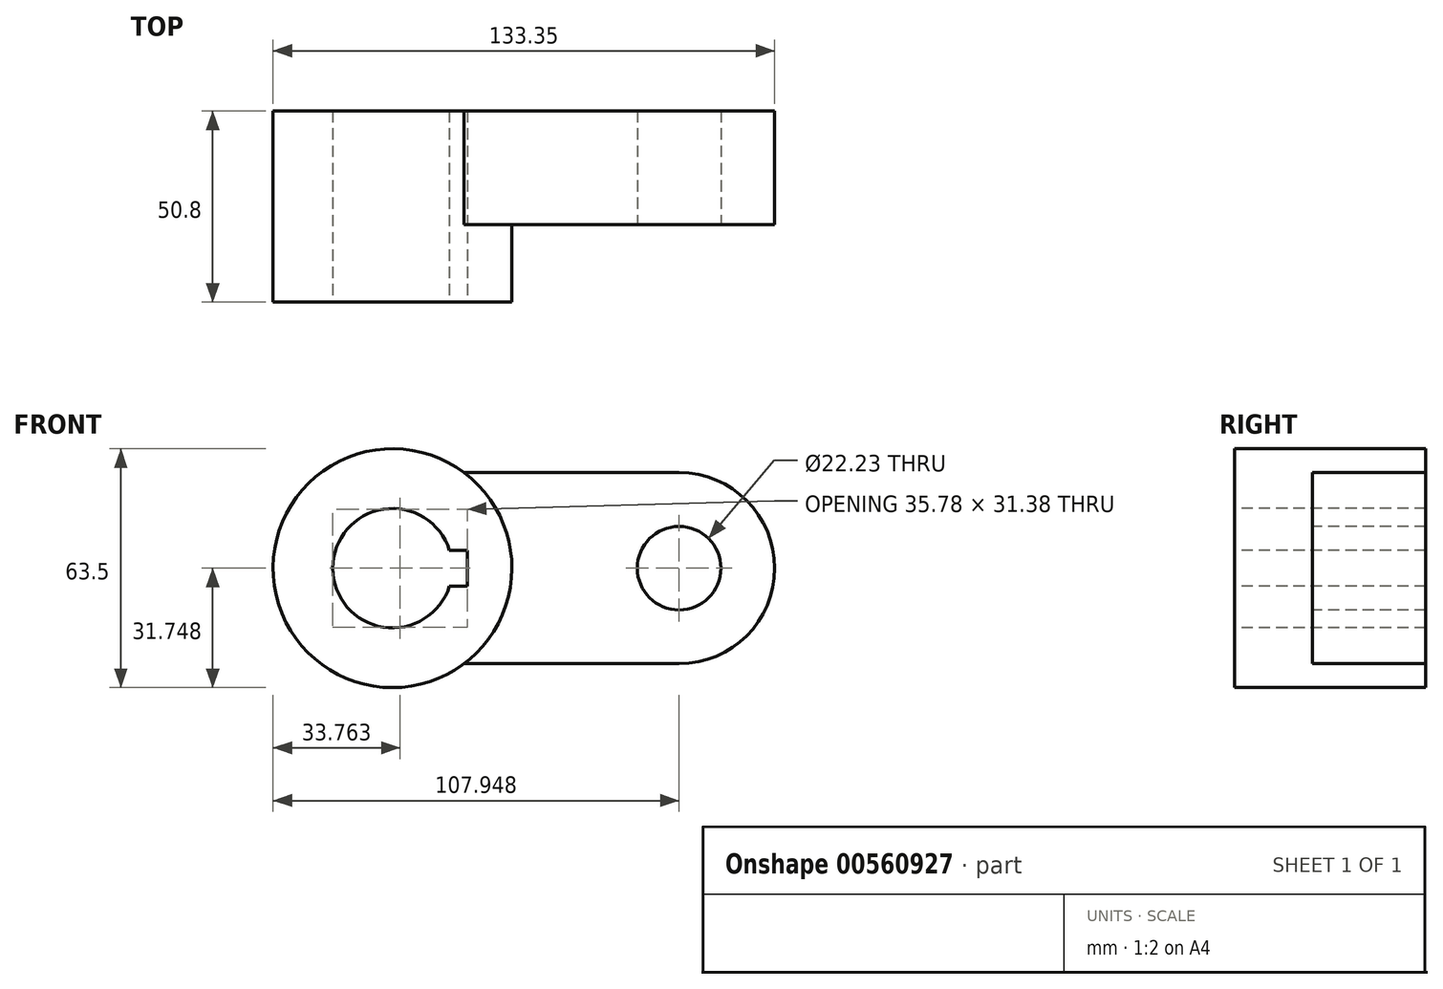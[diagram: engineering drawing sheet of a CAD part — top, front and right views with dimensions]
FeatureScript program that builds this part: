
annotation { "Feature Type Name" : "Feature", "Feature Type Description" : "" }
export const myFeature = defineFeature(function(context is Context, id is Id, definition is map)
    precondition{}
    {
        {
            var Q0;
            Q0=qCreatedBy(makeId("Front.planeOp"),FACE);
            var sketch = newSketch(context, id + "F0", { "sketchPlane" : qUnion([Q0])});
            skLineSegment(sketch, "E0.bottom", {"start": v(-31.26, 34.66) * mm, "end": v(44.94, 34.66) * mm});
            skLineSegment(sketch, "E0.top", {"start": v(-31.26, -16.14) * mm, "end": v(44.94, -16.14) * mm});
            skLineSegment(sketch, "E0.left", {"start": v(-31.26, 34.66) * mm, "end": v(-31.26, -16.14) * mm});
            skLineSegment(sketch, "E0.right", {"start": v(44.94, 34.66) * mm, "end": v(44.94, -16.14) * mm});
            skSolve(sketch);
        }
        {
            var Q0;
            Q0 = qSketchRegion(id + "F0", true);
            extrude(context, id + "F1", {"entities" : qUnion([Q0]), "depth" : 30.16 * mm, "offsetDistance" : 25.4 * mm});
        }
        {
            var Q0;
            Q0=makeQuery(id+"F1.opExtrude","CAP_FACE",FACE,{"disambiguationData":[OSD([sQuery(id+"F0.wireOp",EDGE,"E0.bottom"),sQuery(id+"F0.wireOp",EDGE,"E0.top"),sQuery(id+"F0.wireOp",EDGE,"E0.left"),sQuery(id+"F0.wireOp",EDGE,"E0.right")])],"isStart":true});
            var sketch = newSketch(context, id + "F2", { "sketchPlane" : qUnion([Q0])});
            skArc(sketch, "E1", {"start": v(-44.94, 34.66) * mm, "mid": v(-70.34, 9.26) * mm, "end": v(-44.94, -16.14) * mm});
            skSolve(sketch);
        }
        {
            var Q0;
            Q0=makeQuery(id+"F2.imprint","IMPRINT",FACE,{"disambiguationData":[TD([[makeQuery(id+"F2.imprint","IMPRINT",EDGE,{"derivedFrom":sQuery(id+"F2.wireOp",EDGE,"E1")}),1.0]])]});
            extrude(context, id + "F3", {"entities" : qUnion([Q0]), "operationType" : NewBodyOperationType.ADD, "oppositeDirection" : true, "depth" : 30.16 * mm, "offsetDistance" : 25.4 * mm});
        }
        {
            var Q0;
            {var subQ0=sQuery(id+"F0.wireOp",EDGE,"E0.right");Q0=makeQuery(id+"F3.boolean.opBoolean","MERGE",FACE,{"derivedFrom":[makeQuery(id+"F1.opExtrude","CAP_FACE",FACE,{"disambiguationData":[OSD([sQuery(id+"F0.wireOp",EDGE,"E0.bottom"),sQuery(id+"F0.wireOp",EDGE,"E0.top"),sQuery(id+"F0.wireOp",EDGE,"E0.left"),subQ0])],"isStart":false}),makeQuery(id+"F3.opExtrude","CAP_FACE",FACE,{"disambiguationData":[OSD([subQ0,sQuery(id+"F2.wireOp",EDGE,"E1")])],"isStart":false})]});}
            var sketch = newSketch(context, id + "F4", { "sketchPlane" : qUnion([Q0])});
            skCircle(sketch, "E2", {"center": v(44.94, 9.26) * mm, "radius": 11.11 * mm});
            skSolve(sketch);
        }
        {
            var Q0;
            Q0=makeQuery(id+"F4.imprint","IMPRINT",FACE,{"disambiguationData":[TD([[makeQuery(id+"F4.imprint","IMPRINT",EDGE,{"derivedFrom":sQuery(id+"F4.wireOp",EDGE,"E2")}),1.0]])]});
            extrude(context, id + "F5", {"entities" : qUnion([Q0]), "operationType" : NewBodyOperationType.REMOVE, "oppositeDirection" : true, "depth" : 30.16 * mm, "offsetDistance" : 25.4 * mm});
        }
        {
            var Q0;
            {var subQ0=sQuery(id+"F0.wireOp",EDGE,"E0.right");Q0=makeQuery(id+"F3.boolean.opBoolean","MERGE",FACE,{"derivedFrom":[makeQuery(id+"F1.opExtrude","CAP_FACE",FACE,{"disambiguationData":[OSD([sQuery(id+"F0.wireOp",EDGE,"E0.bottom"),sQuery(id+"F0.wireOp",EDGE,"E0.top"),sQuery(id+"F0.wireOp",EDGE,"E0.left"),subQ0])],"isStart":false}),makeQuery(id+"F3.opExtrude","CAP_FACE",FACE,{"disambiguationData":[OSD([subQ0,sQuery(id+"F2.wireOp",EDGE,"E1")])],"isStart":false})]});}
            var sketch = newSketch(context, id + "F6", { "sketchPlane" : qUnion([Q0])});
            skCircle(sketch, "E3", {"center": v(-31.26, 9.26) * mm, "radius": 31.75 * mm});
            skSolve(sketch);
        }
        {
            var Q0;
            {var subQ5=makeQuery(id+"F1.opExtrude","CAP_EDGE",EDGE,{"disambiguationData":[OSD([sQuery(id+"F0.wireOp",EDGE,"E0.left")])],"isStart":false});Q0=makeQuery(id+"F6.imprint","IMPRINT",FACE,{"disambiguationData":[TD([[makeQuery(id+"F6.imprint","IMPRINT",EDGE,{"derivedFrom":subQ5}),-1.0]])]});}
            var Q1;
            {var subQ5=makeQuery(id+"F1.opExtrude","CAP_EDGE",EDGE,{"disambiguationData":[OSD([sQuery(id+"F0.wireOp",EDGE,"E0.left")])],"isStart":false});Q1=makeQuery(id+"F6.imprint","IMPRINT",FACE,{"disambiguationData":[TD([[makeQuery(id+"F6.imprint","IMPRINT",EDGE,{"derivedFrom":subQ5}),1.0]])]});}
            extrude(context, id + "F7", {"entities" : qUnion([Q0, Q1]), "operationType" : NewBodyOperationType.ADD, "depth" : 20.64 * mm, "offsetDistance" : 25.4 * mm});
        }
        {
            var Q0;
            Q0=makeQuery(id+"F7.opExtrude","CAP_FACE",FACE,{"disambiguationData":[OSD([sQuery(id+"F6.wireOp",EDGE,"E3")])],"isStart":true});
            extrude(context, id + "F8", {"entities" : qUnion([Q0]), "operationType" : NewBodyOperationType.ADD, "depth" : 30.16 * mm, "offsetDistance" : 25.4 * mm});
        }
        {
            var Q0;
            Q0=makeQuery(id+"F7.opExtrude","CAP_FACE",FACE,{"disambiguationData":[OSD([sQuery(id+"F6.wireOp",EDGE,"E3")])],"isStart":false});
            var sketch = newSketch(context, id + "F9", { "sketchPlane" : qUnion([Q0])});
            skCircle(sketch, "E4", {"center": v(-31.26, 9.26) * mm, "radius": 15.88 * mm});
            skSolve(sketch);
        }
        {
            var Q0;
            Q0=makeQuery(id+"F9.imprint","IMPRINT",FACE,{"disambiguationData":[TD([[makeQuery(id+"F9.imprint","IMPRINT",EDGE,{"derivedFrom":sQuery(id+"F9.wireOp",EDGE,"E4")}),1.0]])]});
            extrude(context, id + "F10", {"entities" : qUnion([Q0]), "operationType" : NewBodyOperationType.REMOVE, "oppositeDirection" : true, "depth" : 50.8 * mm, "offsetDistance" : 25.4 * mm});
        }
        {
            var Q0;
            Q0=makeQuery(id+"F7.opExtrude","CAP_FACE",FACE,{"disambiguationData":[OSD([sQuery(id+"F6.wireOp",EDGE,"E3")])],"isStart":false});
            var sketch = newSketch(context, id + "F11", { "sketchPlane" : qUnion([Q0])});
            skLineSegment(sketch, "E5", {"start": v(-16.12, 14.02) * mm, "end": v(-16.12, 4.5) * mm});
            skLineSegment(sketch, "E6", {"start": v(-16.12, 14.02) * mm, "end": v(-11.36, 14.02) * mm});
            skLineSegment(sketch, "E7", {"start": v(-11.36, 14.02) * mm, "end": v(-11.36, 4.5) * mm});
            skLineSegment(sketch, "E8", {"start": v(-11.36, 4.5) * mm, "end": v(-16.12, 4.5) * mm});
            skSolve(sketch);
        }
        {
            var Q0;
            {var subQ0=sQuery(id+"F11.wireOp",EDGE,"E6");Q0=makeQuery(id+"F11.imprint","IMPRINT",FACE,{"disambiguationData":[TD([[makeQuery(id+"F11.imprint","IMPRINT",EDGE,{"derivedFrom":subQ0}),-1.0]])]});}
            extrude(context, id + "F12", {"entities" : qUnion([Q0]), "operationType" : NewBodyOperationType.REMOVE, "oppositeDirection" : true, "depth" : 50.8 * mm, "offsetDistance" : 25.4 * mm});
        }
    });
